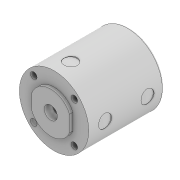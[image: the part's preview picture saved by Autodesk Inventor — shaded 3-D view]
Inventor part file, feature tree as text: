
AUTODESK INVENTOR PART (.ipt)
format: ipt  version: 2020 (Build 240168000, 168)  size: 178,688 bytes
history: native  units: mm
features: extrude x6, sketch x6, other x3, pattern_circular x1, fillet x1, projected_geometry x1
ambient origin geometry x8: Origin, YZ Plane, XZ Plane, XY Plane, X Axis, Y Axis, Z Axis, Center Point
bodies: Body1 (feature_tree)
feature tree (18):
  other  "솔리드1"
  extrude  "돌출1"  Depth=42.4mm
  extrude  "돌출2"  Depth=45.9mm TaperAngle=0.0deg
  extrude  "돌출3"  Depth=40.0mm TaperAngle=360.0deg
  extrude  "돌출4"  Depth=6.0mm TaperAngle=0.0deg
  other  "작업 평면1"
  extrude  "돌출5"  Depth=40.0mm TaperAngle=360.0deg
  other  "작업 평면5"
  extrude  "돌출7"  Depth=2.0mm TaperAngle=0.0deg
  pattern_circular  "원형 패턴2"  [2 undecoded]
  fillet  "모깎기1"  Radius=5.0mm
  sketch  "스케치1"
  sketch  "스케치2"
  sketch  "스케치3"
  sketch  "스케치4"
  sketch  "스케치5"
  projected_geometry  "투영된 루프1"
  sketch  "스케치7"
note: 2 required parameter values undecoded (feature->parameter linkage not recoverable at this tier; creation-order binding heuristic only, values carry confidence <= 0.55)
